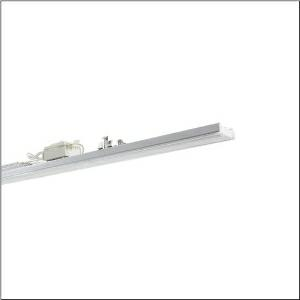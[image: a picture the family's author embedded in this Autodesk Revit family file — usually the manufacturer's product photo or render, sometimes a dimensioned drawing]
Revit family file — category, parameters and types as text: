
# Revit family: licross_r__21_recessed_ho_52tl1emn4e5s_ecfe
name_source: partatom
category: Lighting Fixtures
units: mm (PartAtom-declared; Revit-internal decimal feet)

## family parameters
Cut with Voids When Loaded = No
Host = Face
Light Source = No
Part Type = Normal
Room Calculation Point = No
Round Connector Dimension = Use Diameter
Shared = No

## types (1)
- --- (1 x LED, 14710 lm, 83.1 W, 4000K)
    Apparent Load = 83 VA
    CIE Flux Codes = 85 95 99 100 100
    Color Rendering = 80
    Color Temperature = 4000K
    Default Elevation = 1800 mm
    Description = Licross® 21 Recessed HO, luminaire insert, of sheet steel, galvanised, coil coated, white, length: 1.500mm, width: 66mm, height: 67mm, LED rated luminous flux: 14.710lm, light colour: 840, control gear: ON/OFF Multilumen, with plug, 3-pole, with phase selection, mains connection: 220..240V, AC, 50/60Hz, rated input power: 83W, halogen-free wiring, primary light control with lens, of plastic, primary optical cover: cover, of PMMA, light emission: direct distribution, primary light characteristic: symmetric, protection rating (complete): IP40, insulation class (complete): insulation class I (protective earthing), certification: CE, ENEC, VDE, UKCA, protection symbol: D if used in an environment without relevant dust loads with corresponding accessories, impact resistance: IK06, permissible ambient temperature for indoor applications: -35..+30°C, corresponds to IFS (International Featured Standards) requirements for safety and quality in the food industry, reducing of maximum allowable ambient temperature of 5°C with ceiling mounting, LABS conformity tested according to VDMA 24364:2018-05, packaging unit: 1 piece
    Height = 58 mm
    Lamp = 1 x LED
    Lamp Light Flux = 14710 lm
    Lamp Power = 83.1 W
    Lamp count = 1
    Length = 1500 mm
    Luminous efficacy = 177 lm/W
    Manufacturer = Siteco
    ModVariant = No
    Model = 52TL1EMN4E5S
    Mounting Place = Ceiling
    Mounting Type = Pendant
    Number of Poles = 1
    OnlyDefault = Yes
    Power Factor = 1
    Product Name = Licross® 21 Recessed HO
    Product group = luminaire insert
    ProductGroupID = 902
    Protection Class = Protection class I
    Protection Degree = IP 40
    RLX_Detail_Level = 1
    RLX_Emergency_Light_Flux = 0 lm
    RLX_Emergency_Type = 0
    RLX_Emergency_Type_DB = No
    RlxData = <blob elided: 22365 chars, md5=735942ea>
    Socket = socket
    Standby Power = 0 W
    System Light Flux = 14710 lm
    System Power = 83 W
    Type Comments = factory setting: luminous flux: 100 % | (A | C | E) | 195 mA
    Type Image = l_1296930.jpg
    URL = http://relux.com
    VarID = @adj_106494
    Voltage = 0 V
    Weight = 0.00 kg
    Width = 66 mm

## geometry (parser evidence)
native form markers: Blend x4, Sweep x13
no freeform markers — native parametric forms only
